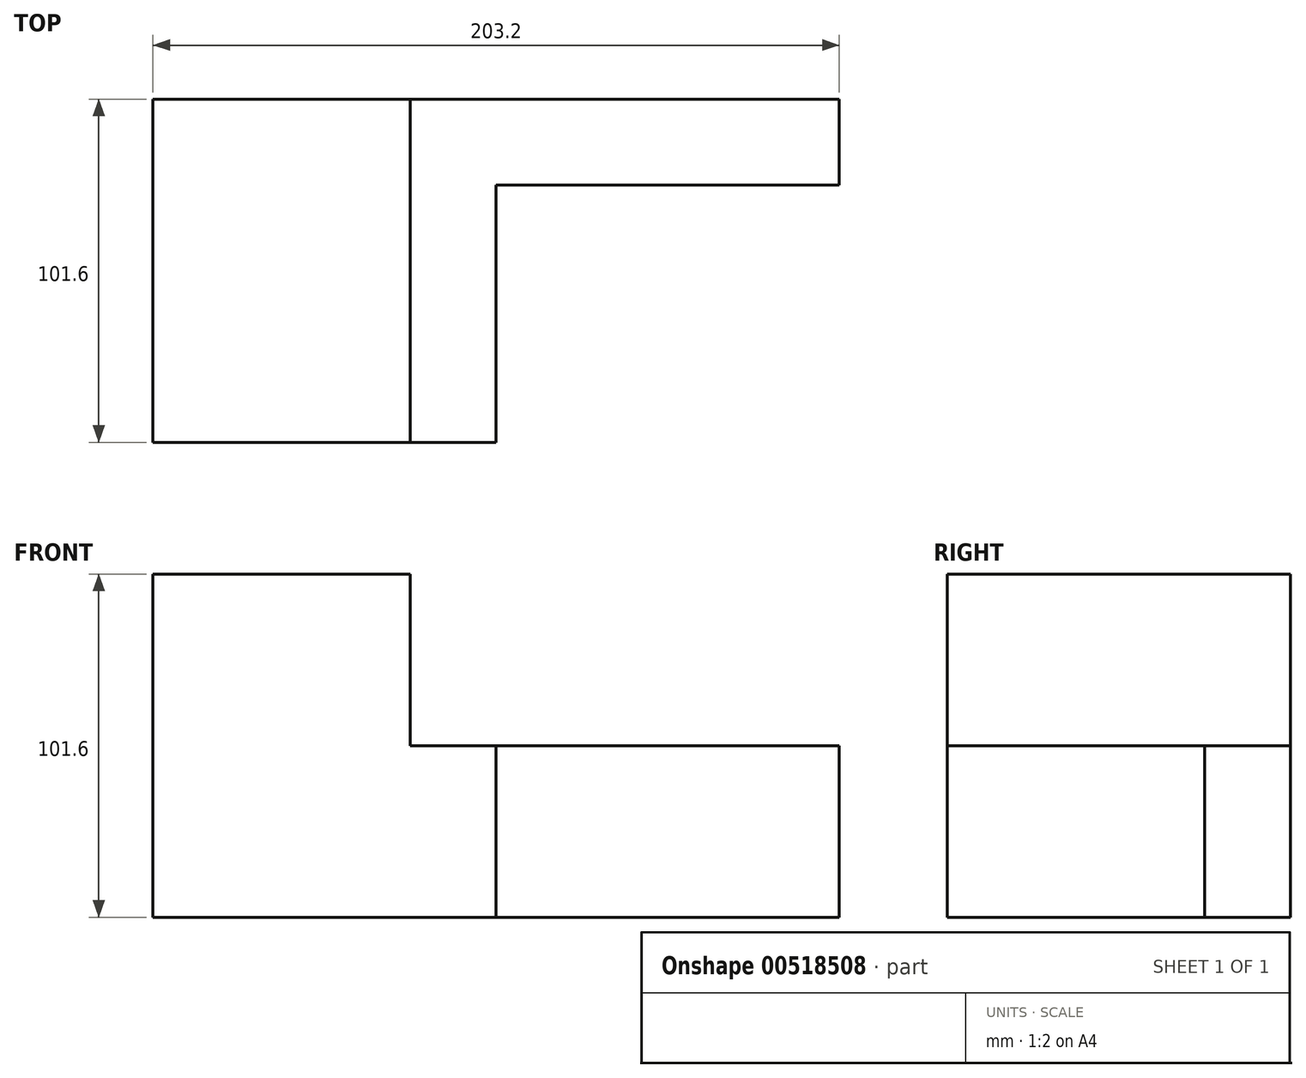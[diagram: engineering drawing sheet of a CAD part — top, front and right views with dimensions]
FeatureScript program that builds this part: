
annotation { "Feature Type Name" : "Feature", "Feature Type Description" : "" }
export const myFeature = defineFeature(function(context is Context, id is Id, definition is map)
    precondition{}
    {
        {
            var Q0;
            Q0=qCreatedBy(makeId("Front.planeOp"),FACE);
            var sketch = newSketch(context, id + "F0", { "sketchPlane" : qUnion([Q0])});
            skLineSegment(sketch, "E0.bottom", {"start": v(-76.2, 34.3) * mm, "end": v(0, 34.3) * mm});
            skLineSegment(sketch, "E0.top", {"start": v(-76.2, -67.3) * mm, "end": v(127, -67.3) * mm});
            skLineSegment(sketch, "E0.left", {"start": v(-76.2, 34.3) * mm, "end": v(-76.2, -67.3) * mm});
            skLineSegment(sketch, "E0.right", {"start": v(127, -16.5) * mm, "end": v(127, -67.3) * mm});
            skLineSegment(sketch, "E1.top", {"start": v(70.55, -16.5) * mm, "end": v(0, -16.5) * mm});
            skLineSegment(sketch, "E1.right", {"start": v(0, 34.3) * mm, "end": v(0, -16.5) * mm});
            skLineSegment(sketch, "E2.bottom", {"start": v(0, -16.5) * mm, "end": v(127, -16.5) * mm});
            skLineSegment(sketch, "E2.right", {"start": v(127, -16.5) * mm, "end": v(127, -41.9) * mm});
            skSolve(sketch);
        }
        {
            var Q0;
            Q0=makeQuery(id+"F0.imprint","IMPRINT",FACE,{"disambiguationData":[TD([[makeQuery(id+"F0.imprint","IMPRINT",EDGE,{"derivedFrom":sQuery(id+"F0.wireOp",EDGE,"E0.bottom")}),-1.0]])]});
            extrude(context, id + "F1", {"entities" : qUnion([Q0]), "depth" : 101.6 * mm});
        }
        {
            var Q0;
            Q0=makeQuery(id+"F1.opExtrude","SWEPT_FACE",FACE,{"disambiguationData":[OSD([sQuery(id+"F0.wireOp",EDGE,"E2.bottom")])]});
            var sketch = newSketch(context, id + "F2", { "sketchPlane" : qUnion([Q0])});
            skLineSegment(sketch, "E3.bottom", {"start": v(127, -101.6) * mm, "end": v(27.27, -101.6) * mm});
            skLineSegment(sketch, "E3.left", {"start": v(127, -101.6) * mm, "end": v(127, -28.18) * mm});
            skLineSegment(sketch, "E4.bottom", {"start": v(27.27, -101.6) * mm, "end": v(25.4, -101.6) * mm});
            skLineSegment(sketch, "E4.top", {"start": v(127, -25.4) * mm, "end": v(25.4, -25.4) * mm});
            skLineSegment(sketch, "E4.left", {"start": v(127, -101.6) * mm, "end": v(127, -25.4) * mm});
            skLineSegment(sketch, "E4.right", {"start": v(25.4, -101.6) * mm, "end": v(25.4, -25.4) * mm});
            skSolve(sketch);
        }
        {
            var Q0;
            {var subQ1=sQuery(id+"F2.wireOp",EDGE,"E3.bottom");Q0=makeQuery(id+"F2.imprint","IMPRINT",FACE,{"disambiguationData":[TD([[makeQuery(id+"F2.imprint","IMPRINT",EDGE,{"derivedFrom":subQ1}),1.0]])]});}
            extrude(context, id + "F3", {"entities" : qUnion([Q0]), "operationType" : NewBodyOperationType.REMOVE, "endBound" : BoundingType.THROUGH_ALL, "oppositeDirection" : true, "depth" : 50.8 * mm});
        }
    });
